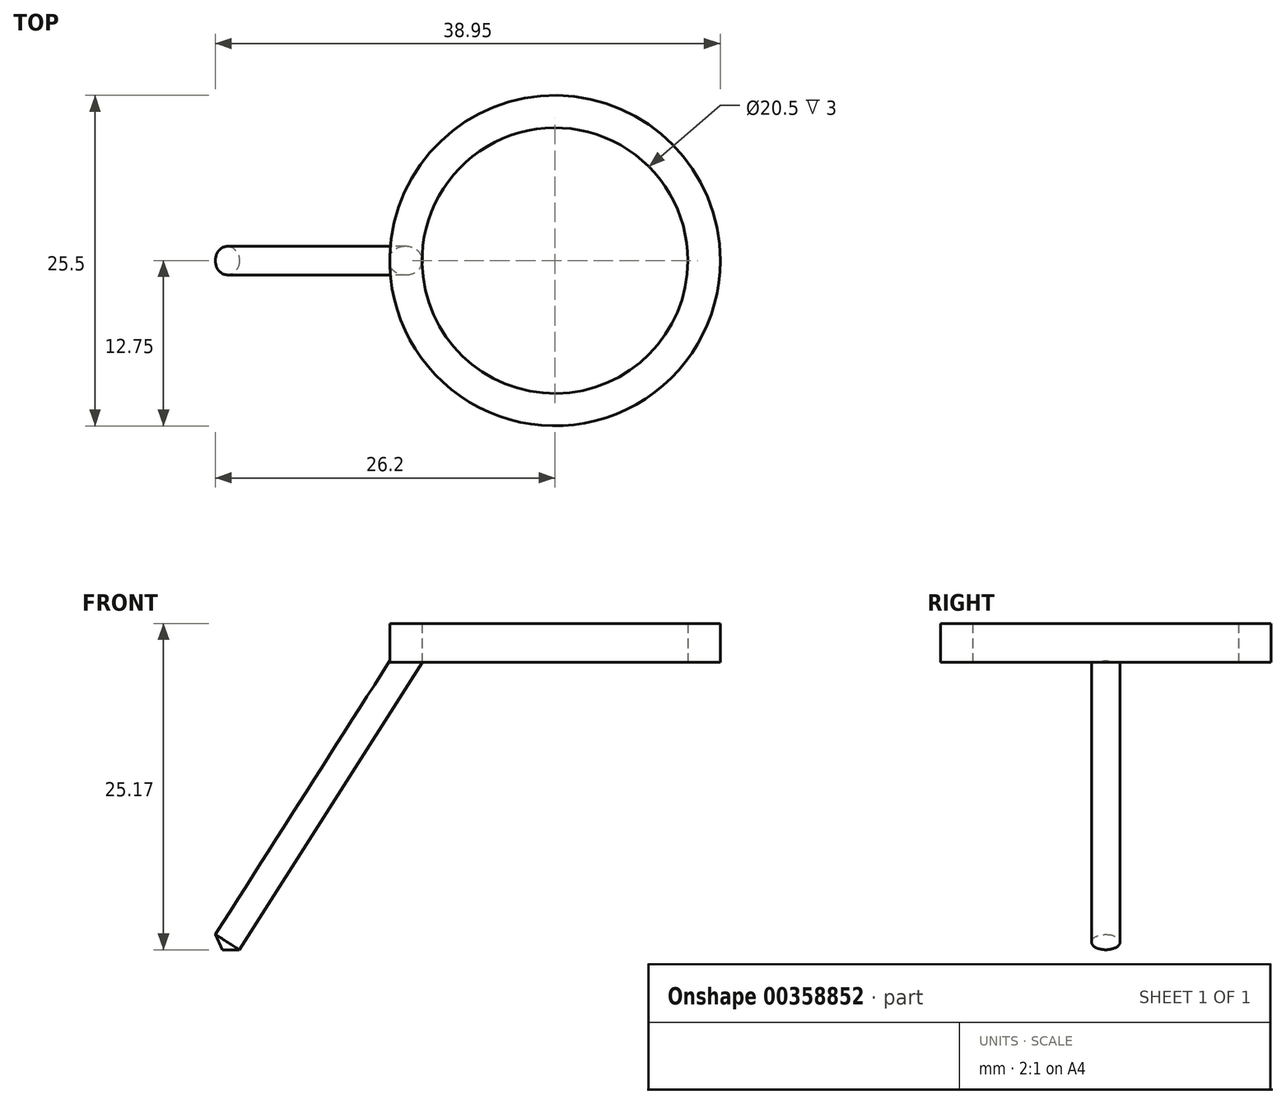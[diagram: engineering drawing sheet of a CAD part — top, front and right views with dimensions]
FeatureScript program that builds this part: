
annotation { "Feature Type Name" : "Feature", "Feature Type Description" : "" }
export const myFeature = defineFeature(function(context is Context, id is Id, definition is map)
    precondition{}
    {
        {
            var Q0;
            Q0=qCreatedBy(makeId("Top.planeOp"),FACE);
            var sketch = newSketch(context, id + "F0", { "sketchPlane" : qUnion([Q0])});
            skCircle(sketch, "E0", {"center": v(0, 0) * mm, "radius": 10.25 * mm});
            skCircle(sketch, "E1", {"center": v(0, 0) * mm, "radius": 12.75 * mm});
            skSolve(sketch);
        }
        {
            var Q0;
            Q0=makeQuery(id+"F0.imprint","IMPRINT",FACE,{"disambiguationData":[TD([[makeQuery(id+"F0.imprint","IMPRINT",EDGE,{"derivedFrom":sQuery(id+"F0.wireOp",EDGE,"E0")}),-1.0]])]});
            extrude(context, id + "F1", {"entities" : qUnion([Q0]), "depth" : 3 * mm});
        }
        {
            var Q0;
            Q0=qCreatedBy(makeId("Front.planeOp"),FACE);
            var sketch = newSketch(context, id + "F2", { "sketchPlane" : qUnion([Q0])});
            skLineSegment(sketch, "E2", {"start": v(-12.83, 0) * mm, "end": v(-26.95, -22.17) * mm});
            skLineSegment(sketch, "E3", {"start": v(-26.95, -22.17) * mm, "end": v(-24.35, -22.17) * mm});
            skLineSegment(sketch, "E4", {"start": v(-24.35, -22.17) * mm, "end": v(-10.22, 0) * mm});
            skLineSegment(sketch, "E5", {"start": v(-10.22, 0) * mm, "end": v(-12.83, 0) * mm});
            skLineSegment(sketch, "E6", {"start": v(-25.65, -22.17) * mm, "end": v(-11.52, 0) * mm});
            skSolve(sketch);
        }
        {
            var Q0;
            {var subQ0=sQuery(id+"F2.wireOp",EDGE,"E4");Q0=makeQuery(id+"F2.imprint","IMPRINT",FACE,{"disambiguationData":[TD([[makeQuery(id+"F2.imprint","IMPRINT",EDGE,{"derivedFrom":subQ0}),1.0]])]});}
            var Q1;
            Q1=sQuery(id+"F2.wireOp",EDGE,"E6");
            revolve(context, id + "F3", {"operationType" : NewBodyOperationType.ADD, "entities" : qUnion([Q0]), "axis" : qUnion([Q1]), "revolveType" : RevolveType.FULL});
        }
    });
